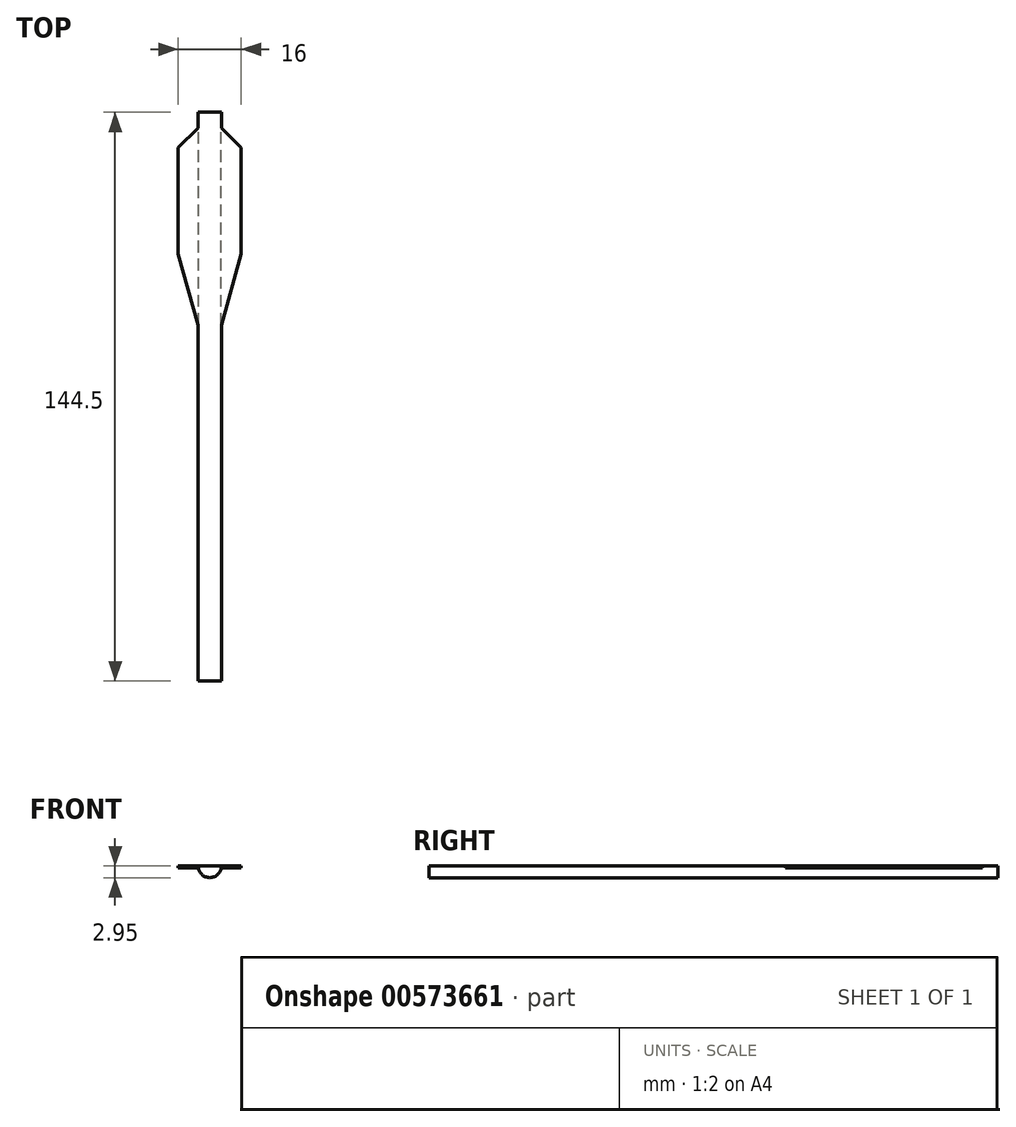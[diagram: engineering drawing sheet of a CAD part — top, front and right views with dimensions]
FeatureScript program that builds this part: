
annotation { "Feature Type Name" : "Feature", "Feature Type Description" : "" }
export const myFeature = defineFeature(function(context is Context, id is Id, definition is map)
    precondition{}
    {
        {
            var Q0;
            Q0=qCreatedBy(makeId("Front.planeOp"),FACE);
            var sketch = newSketch(context, id + "F0", { "sketchPlane" : qUnion([Q0])});
            skCircle(sketch, "E0", {"center": v(0, 0) * mm, "radius": 2.95 * mm});
            skLineSegment(sketch, "E1", {"start": v(-2.95, 0) * mm, "end": v(2.95, 0) * mm});
            skSolve(sketch);
        }
        {
            var Q0;
            {var subQ0=sQuery(id+"F0.wireOp",EDGE,"E1");Q0=makeQuery(id+"F0.imprint","IMPRINT",FACE,{"disambiguationData":[TD([[makeQuery(id+"F0.imprint","IMPRINT",EDGE,{"derivedFrom":subQ0}),-1.0]])]});}
            extrude(context, id + "F1", {"entities" : qUnion([Q0]), "depth" : 144.5 * mm, "offsetDistance" : 25 * mm});
        }
        {
            var Q0;
            Q0=qCreatedBy(makeId("Right.planeOp"),FACE);
            var sketch = newSketch(context, id + "F2", { "sketchPlane" : qUnion([Q0])});
            skLineSegment(sketch, "E2", {"start": v(0, 0) * mm, "end": v(-54, 0) * mm});
            skLineSegment(sketch, "E3", {"start": v(0, 0) * mm, "end": v(-4, 0) * mm});
            skLineSegment(sketch, "E4", {"start": v(-4, 0) * mm, "end": v(-4, 0.5) * mm});
            skLineSegment(sketch, "E5", {"start": v(-4, 0.5) * mm, "end": v(-54, 0.5) * mm});
            skLineSegment(sketch, "E6", {"start": v(-54, 0) * mm, "end": v(-54, 0.5) * mm});
            skLineSegment(sketch, "E7", {"start": v(-54, 0) * mm, "end": v(-54, -0.5) * mm});
            skLineSegment(sketch, "E8", {"start": v(-54, -0.5) * mm, "end": v(-4, -0.5) * mm});
            skLineSegment(sketch, "E9", {"start": v(-4, -0.5) * mm, "end": v(-4, 0) * mm});
            skSolve(sketch);
        }
        {
            var Q0;
            Q0=makeQuery(id+"F2.imprint","IMPRINT",FACE,{"disambiguationData":[TD([[makeQuery(id+"F2.imprint","IMPRINT",EDGE,{"derivedFrom":sQuery(id+"F2.wireOp",EDGE,"E2")}),-1.0]])]});
            extrude(context, id + "F3", {"entities" : qUnion([Q0]), "operationType" : NewBodyOperationType.ADD, "depth" : 8 * mm, "offsetDistance" : 25 * mm, "hasSecondDirection" : true, "secondDirectionOppositeDirection" : true, "secondDirectionDepth" : 8 * mm});
        }
        {
            var Q0;
            {var subQ0=sQuery(id+"F2.wireOp",EDGE,"E4");var subQ1=sQuery(id+"F2.wireOp",EDGE,"E6");var subQ2=sQuery(id+"F2.wireOp",EDGE,"E2");Q0=makeQuery(id+"F3.boolean.opBoolean","SPLIT",FACE,{"disambiguationData":[TD([makeQuery(id+"F3.opExtrude","CAP_FACE",FACE,{"disambiguationData":[OSD([subQ2,subQ0,sQuery(id+"F2.wireOp",EDGE,"E5"),subQ1])],"isStart":false})])],"derivedFrom":makeQuery(id+"F3.opExtrude","SWEPT_FACE",FACE,{"disambiguationData":[OSD([subQ2])]})});}
            var Q1;
            {var subQ0=sQuery(id+"F2.wireOp",EDGE,"E4");var subQ1=sQuery(id+"F2.wireOp",EDGE,"E6");var subQ2=sQuery(id+"F2.wireOp",EDGE,"E2");Q1=makeQuery(id+"F3.boolean.opBoolean","SPLIT",FACE,{"disambiguationData":[TD([makeQuery(id+"F3.opExtrude","CAP_FACE",FACE,{"disambiguationData":[OSD([subQ2,subQ0,sQuery(id+"F2.wireOp",EDGE,"E5"),subQ1])],"isStart":true})])],"derivedFrom":makeQuery(id+"F3.opExtrude","SWEPT_FACE",FACE,{"disambiguationData":[OSD([subQ2])]})});}
            extrude(context, id + "F4", {"entities" : qUnion([Q0, Q1]), "operationType" : NewBodyOperationType.ADD, "depth" : .5 * mm, "offsetDistance" : 25 * mm});
        }
        {
            var Q0;
            {var subQ0=sQuery(id+"F0.wireOp",EDGE,"E0");var subQ1=sQuery(id+"F0.wireOp",EDGE,"E1");Q0=makeQuery(id+"F4.opExtrude","SWEPT_FACE",FACE,{"disambiguationData":[OSD([subQ0,subQ1]),TDD([makeQuery(id+"F3.boolean.opBoolean","SPLIT",EDGE,{"disambiguationData":[topologyDisambiguationEdgeConnected([makeQuery(id+"F1.opExtrude","SWEPT_FACE",FACE,{"disambiguationData":[OSD([subQ0])]}),makeQuery(id+"F3.opExtrude","SWEPT_FACE",FACE,{"disambiguationData":[OSD([sQuery(id+"F2.wireOp",EDGE,"E2")])]})])],"derivedFrom":makeQuery(id+"F1.opExtrude","SWEPT_EDGE",EDGE,{"disambiguationData":[OSD([subQ0,subQ1]),TDD([makeQuery(id+"F0.imprint","INTERSECT",VERTEX,{"disambiguationData":[OD(1.0)],"derivedFrom":[subQ0,subQ1]})])]})})])]});}
            extrude(context, id + "F5", {"entities" : qUnion([Q0]), "operationType" : NewBodyOperationType.ADD, "depth" : 6 * mm, "offsetDistance" : 25 * mm});
        }
        {
            var Q0;
            Q0=makeQuery(id+"F3.opExtrude","SWEPT_FACE",FACE,{"disambiguationData":[OSD([sQuery(id+"F2.wireOp",EDGE,"E5")])]});
            extrude(context, id + "F6", {"entities" : qUnion([Q0]), "operationType" : NewBodyOperationType.REMOVE, "oppositeDirection" : true, "depth" : .5 * mm, "offsetDistance" : 25 * mm});
        }
        {
            var Q0;
            {var subQ2=sQuery(id+"F0.wireOp",EDGE,"E1");var subQ4=makeQuery(id+"F1.opExtrude","SWEPT_FACE",FACE,{"disambiguationData":[OSD([subQ2])]});Q0=makeQuery(id+"F6.boolean.opBoolean","MERGE",FACE,{"derivedFrom":[makeQuery(id+"F3.boolean.opBoolean","SPLIT",FACE,{"disambiguationData":[TD([makeQuery(id+"F3.opExtrude","SWEPT_FACE",FACE,{"disambiguationData":[OSD([sQuery(id+"F2.wireOp",EDGE,"E4")])]})])],"derivedFrom":subQ4}),makeQuery(id+"F3.boolean.opBoolean","SPLIT",FACE,{"disambiguationData":[TD([makeQuery(id+"F3.opExtrude","SWEPT_FACE",FACE,{"disambiguationData":[OSD([sQuery(id+"F2.wireOp",EDGE,"E6")])]})])],"derivedFrom":subQ4}),makeQuery(id+"F6.opExtrude","CAP_FACE",FACE,{"disambiguationData":[OSD([sQuery(id+"F2.wireOp",EDGE,"E5")])],"isStart":false})]});}
            var sketch = newSketch(context, id + "F7", { "sketchPlane" : qUnion([Q0])});
            skLineSegment(sketch, "E10", {"start": v(2.95, -4) * mm, "end": v(-2.95, -4) * mm});
            skLineSegment(sketch, "E11", {"start": v(-2.95, -4) * mm, "end": v(-2.95, -9) * mm});
            skLineSegment(sketch, "E12", {"start": v(-2.95, -9) * mm, "end": v(2.95, -9) * mm});
            skLineSegment(sketch, "E13", {"start": v(2.95, -9) * mm, "end": v(2.95, -4) * mm});
            skLineSegment(sketch, "E14", {"start": v(-2.95, -9) * mm, "end": v(-8, -9) * mm});
            skLineSegment(sketch, "E15", {"start": v(-8, -9) * mm, "end": v(8, -9) * mm});
            skLineSegment(sketch, "E16", {"start": v(-2.95, -4) * mm, "end": v(-8, -9) * mm});
            skLineSegment(sketch, "E17", {"start": v(8, -9) * mm, "end": v(2.95, -4) * mm});
            skLineSegment(sketch, "E18", {"start": v(2.95, -54) * mm, "end": v(2.95, -36) * mm});
            skLineSegment(sketch, "E19", {"start": v(2.95, -36) * mm, "end": v(-2.95, -36) * mm});
            skLineSegment(sketch, "E20", {"start": v(-2.95, -36) * mm, "end": v(-2.95, -54) * mm});
            skLineSegment(sketch, "E21", {"start": v(2.95, -54) * mm, "end": v(8, -36) * mm});
            skLineSegment(sketch, "E22", {"start": v(8, -36) * mm, "end": v(-8, -36) * mm});
            skLineSegment(sketch, "E23", {"start": v(-8, -36) * mm, "end": v(-2.95, -54) * mm});
            skSolve(sketch);
        }
        {
            var Q0;
            {var subQ0=sQuery(id+"F7.wireOp",EDGE,"E16");Q0=makeQuery(id+"F7.imprint","IMPRINT",FACE,{"disambiguationData":[TD([[makeQuery(id+"F7.imprint","IMPRINT",EDGE,{"derivedFrom":subQ0}),-1.0]])]});}
            var Q1;
            {var subQ0=sQuery(id+"F7.wireOp",EDGE,"E23");Q1=makeQuery(id+"F7.imprint","IMPRINT",FACE,{"disambiguationData":[TD([[makeQuery(id+"F7.imprint","IMPRINT",EDGE,{"derivedFrom":subQ0}),-1.0]])]});}
            var Q2;
            {var subQ0=sQuery(id+"F7.wireOp",EDGE,"E21");Q2=makeQuery(id+"F7.imprint","IMPRINT",FACE,{"disambiguationData":[TD([[makeQuery(id+"F7.imprint","IMPRINT",EDGE,{"derivedFrom":subQ0}),-1.0]])]});}
            var Q3;
            {var subQ0=sQuery(id+"F7.wireOp",EDGE,"E17");Q3=makeQuery(id+"F7.imprint","IMPRINT",FACE,{"disambiguationData":[TD([[makeQuery(id+"F7.imprint","IMPRINT",EDGE,{"derivedFrom":subQ0}),-1.0]])]});}
            extrude(context, id + "F8", {"entities" : qUnion([Q0, Q1, Q2, Q3]), "operationType" : NewBodyOperationType.REMOVE, "oppositeDirection" : true, "depth" : .5 * mm, "offsetDistance" : 25 * mm});
        }
    });
